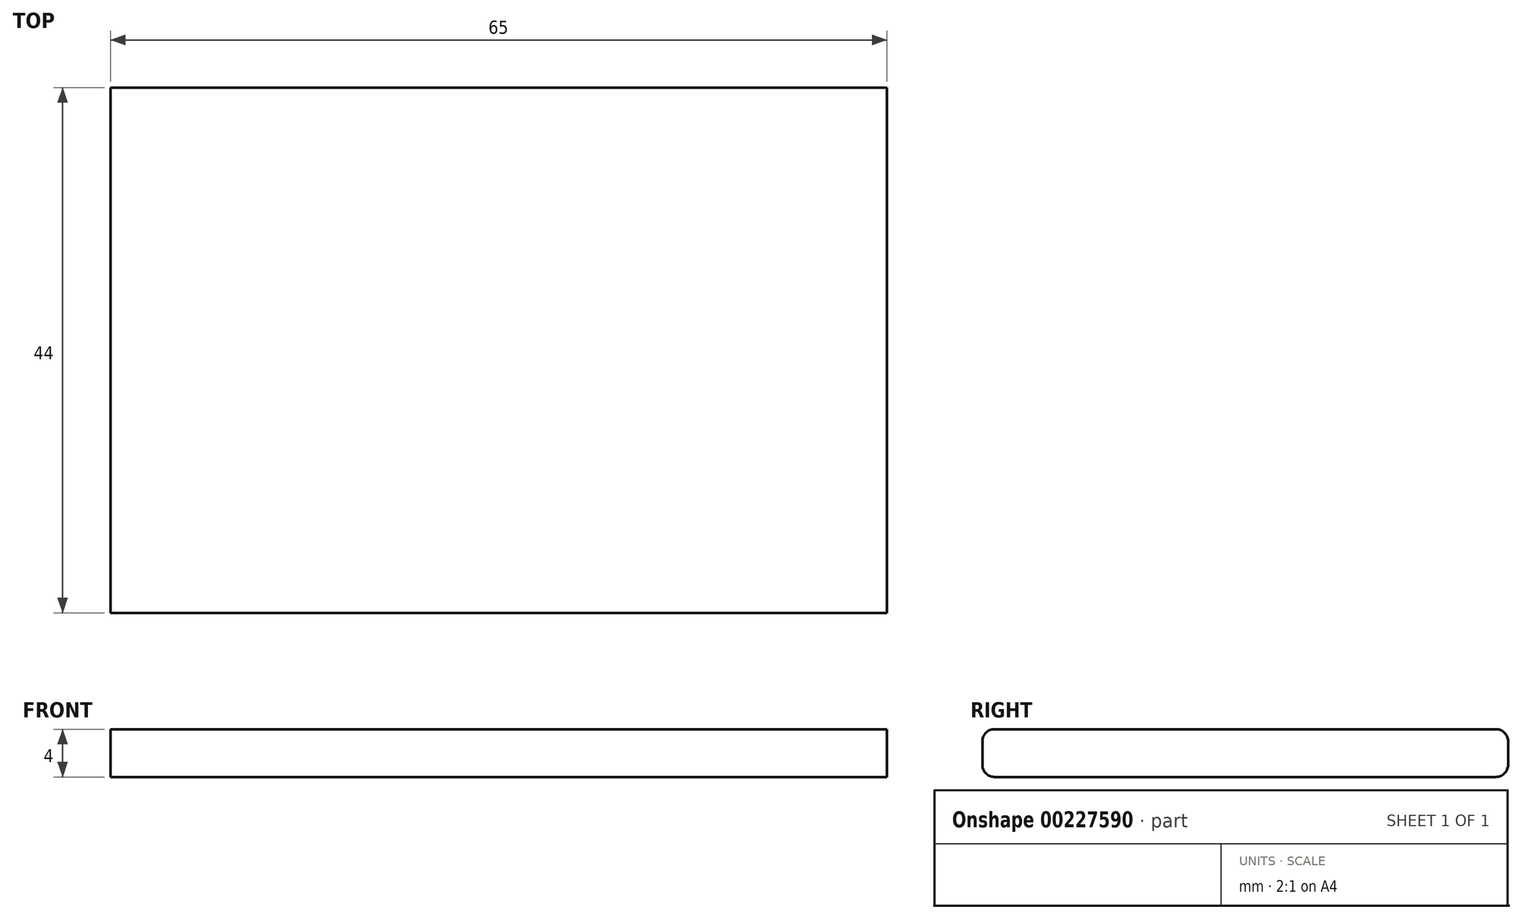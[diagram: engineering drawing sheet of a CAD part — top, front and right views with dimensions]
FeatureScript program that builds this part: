
annotation { "Feature Type Name" : "Feature", "Feature Type Description" : "" }
export const myFeature = defineFeature(function(context is Context, id is Id, definition is map)
    precondition{}
    {
        {
            var Q0;
            Q0=qCreatedBy(makeId("Top.planeOp"),FACE);
            var sketch = newSketch(context, id + "F0", { "sketchPlane" : qUnion([Q0])});
            skLineSegment(sketch, "E0.bottom", {"start": v(-78.5, 44) * mm, "end": v(-13.5, 44) * mm});
            skLineSegment(sketch, "E0.top", {"start": v(-78.5, 0) * mm, "end": v(-13.5, 0) * mm});
            skLineSegment(sketch, "E0.left", {"start": v(-78.5, 44) * mm, "end": v(-78.5, 0) * mm});
            skLineSegment(sketch, "E0.right", {"start": v(-13.5, 44) * mm, "end": v(-13.5, 0) * mm});
            skSolve(sketch);
        }
        {
            var Q0;
            Q0=makeQuery(id+"F0.imprint","IMPRINT",FACE,{"disambiguationData":[TD([[makeQuery(id+"F0.imprint","IMPRINT",EDGE,{"derivedFrom":sQuery(id+"F0.wireOp",EDGE,"E0.bottom")}),-1.0]])]});
            extrude(context, id + "F1", {"entities" : qUnion([Q0]), "depth" : 4 * mm});
        }
        {
            var Q0;
            Q0=makeQuery(id+"F1.opExtrude","CAP_EDGE",EDGE,{"disambiguationData":[OSD([sQuery(id+"F0.wireOp",EDGE,"E0.top")])],"isStart":false});
            var Q1;
            Q1=makeQuery(id+"F1.opExtrude","CAP_EDGE",EDGE,{"disambiguationData":[OSD([sQuery(id+"F0.wireOp",EDGE,"E0.top")])],"isStart":true});
            var Q2;
            Q2=makeQuery(id+"F1.opExtrude","CAP_EDGE",EDGE,{"disambiguationData":[OSD([sQuery(id+"F0.wireOp",EDGE,"E0.bottom")])],"isStart":false});
            var Q3;
            Q3=makeQuery(id+"F1.opExtrude","CAP_EDGE",EDGE,{"disambiguationData":[OSD([sQuery(id+"F0.wireOp",EDGE,"E0.bottom")])],"isStart":true});
            fillet(context, id + "F2", {"entities" : qUnion([Q0, Q1, Q2, Q3]), "radius" : 1 * mm, "tangentPropagation" : true, "allowEdgeOverflow" : false});
        }
    });
